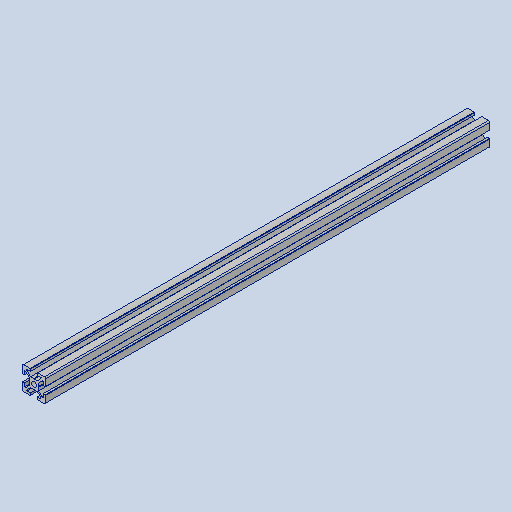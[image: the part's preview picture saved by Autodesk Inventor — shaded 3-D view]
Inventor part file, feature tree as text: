
AUTODESK INVENTOR PART (.ipt)
format: ipt  version: 2024 (Build 280153000, 153)  size: 343,552 bytes
history: native  units: mm
features: other x7, extrude x1, sketch x1
ambient origin geometry x8: Origin, YZ Plane, XZ Plane, XY Plane, X Axis, Y Axis, Z Axis, Center Point
bodies: Solid1 (feature_tree)
feature tree (9):
  extrude  "Extrusion1"  TaperAngle=0.0deg  [1 undecoded]
  other  "to_frame_XY"
  other  "to_frame_YZ"
  other  "to_frame_ZX"
  other  "to_frame_X"
  other  "to_frame_Y"
  other  "to_frame_Z"
  other  "to_frame_Center"
  sketch  "Sketch_5"  dims[d0=380.0mm d1=0.0mm d2=0.0mm]
note: 1 required parameter value undecoded (feature->parameter linkage not recoverable at this tier; creation-order binding heuristic only, values carry confidence <= 0.55)
